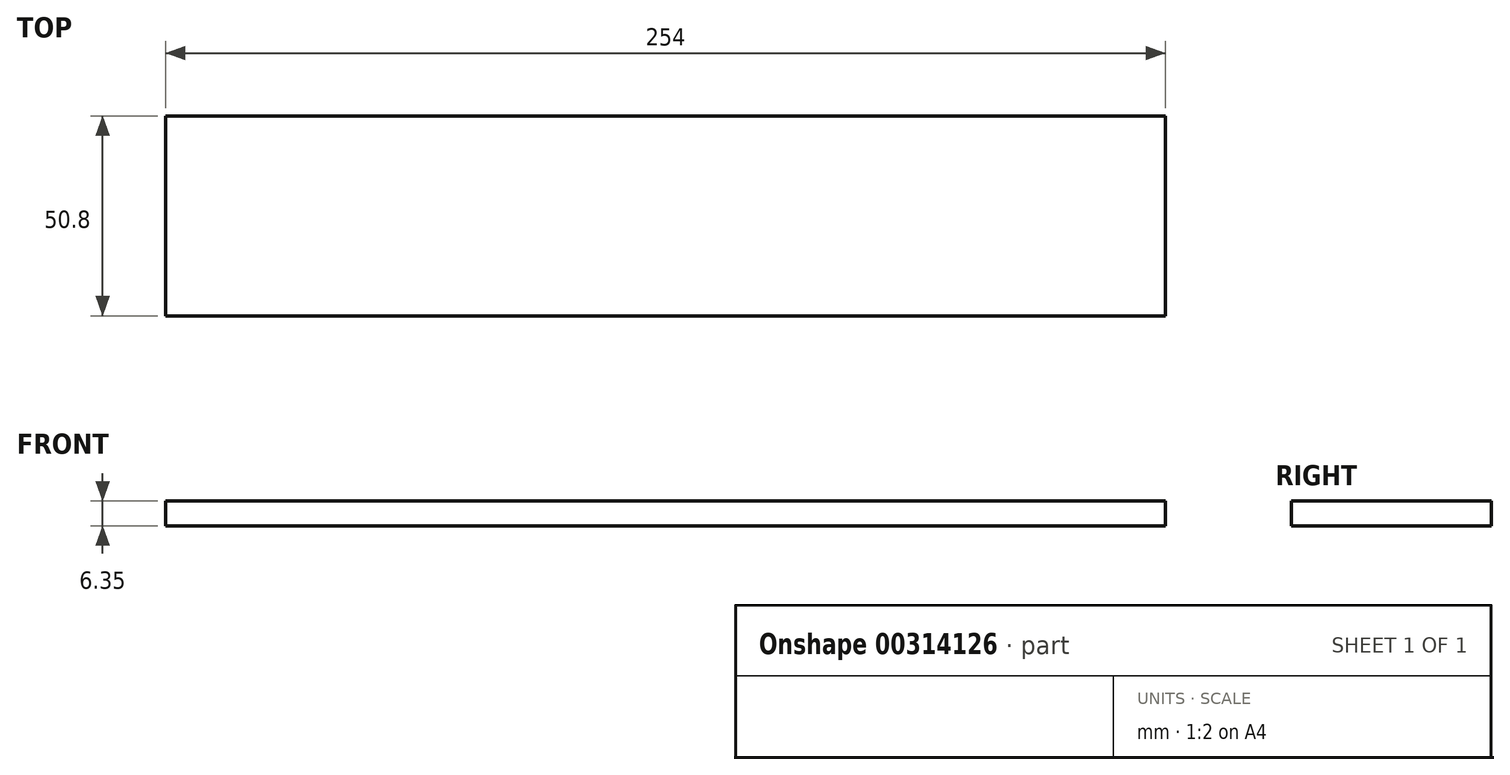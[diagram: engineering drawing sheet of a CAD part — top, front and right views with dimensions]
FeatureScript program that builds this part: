
annotation { "Feature Type Name" : "Feature", "Feature Type Description" : "" }
export const myFeature = defineFeature(function(context is Context, id is Id, definition is map)
    precondition{}
    {
        {
            var Q0;
            Q0=qCreatedBy(makeId("Top.planeOp"),FACE);
            var sketch = newSketch(context, id + "F0", { "sketchPlane" : qUnion([Q0])});
            skLineSegment(sketch, "E0.bottom", {"start": v(0, 0) * mm, "end": v(254, 0) * mm});
            skLineSegment(sketch, "E0.top", {"start": v(0, 50.8) * mm, "end": v(254, 50.8) * mm});
            skLineSegment(sketch, "E0.left", {"start": v(0, 0) * mm, "end": v(0, 50.8) * mm});
            skLineSegment(sketch, "E0.right", {"start": v(254, 0) * mm, "end": v(254, 50.8) * mm});
            skSolve(sketch);
        }
        {
            var Q0;
            Q0=makeQuery(id+"F0.imprint","IMPRINT",FACE,{"disambiguationData":[TD([[makeQuery(id+"F0.imprint","IMPRINT",EDGE,{"derivedFrom":sQuery(id+"F0.wireOp",EDGE,"E0.bottom")}),1.0]])]});
            extrude(context, id + "F1", {"entities" : qUnion([Q0]), "depth" : 6.35 * mm});
        }
    });
